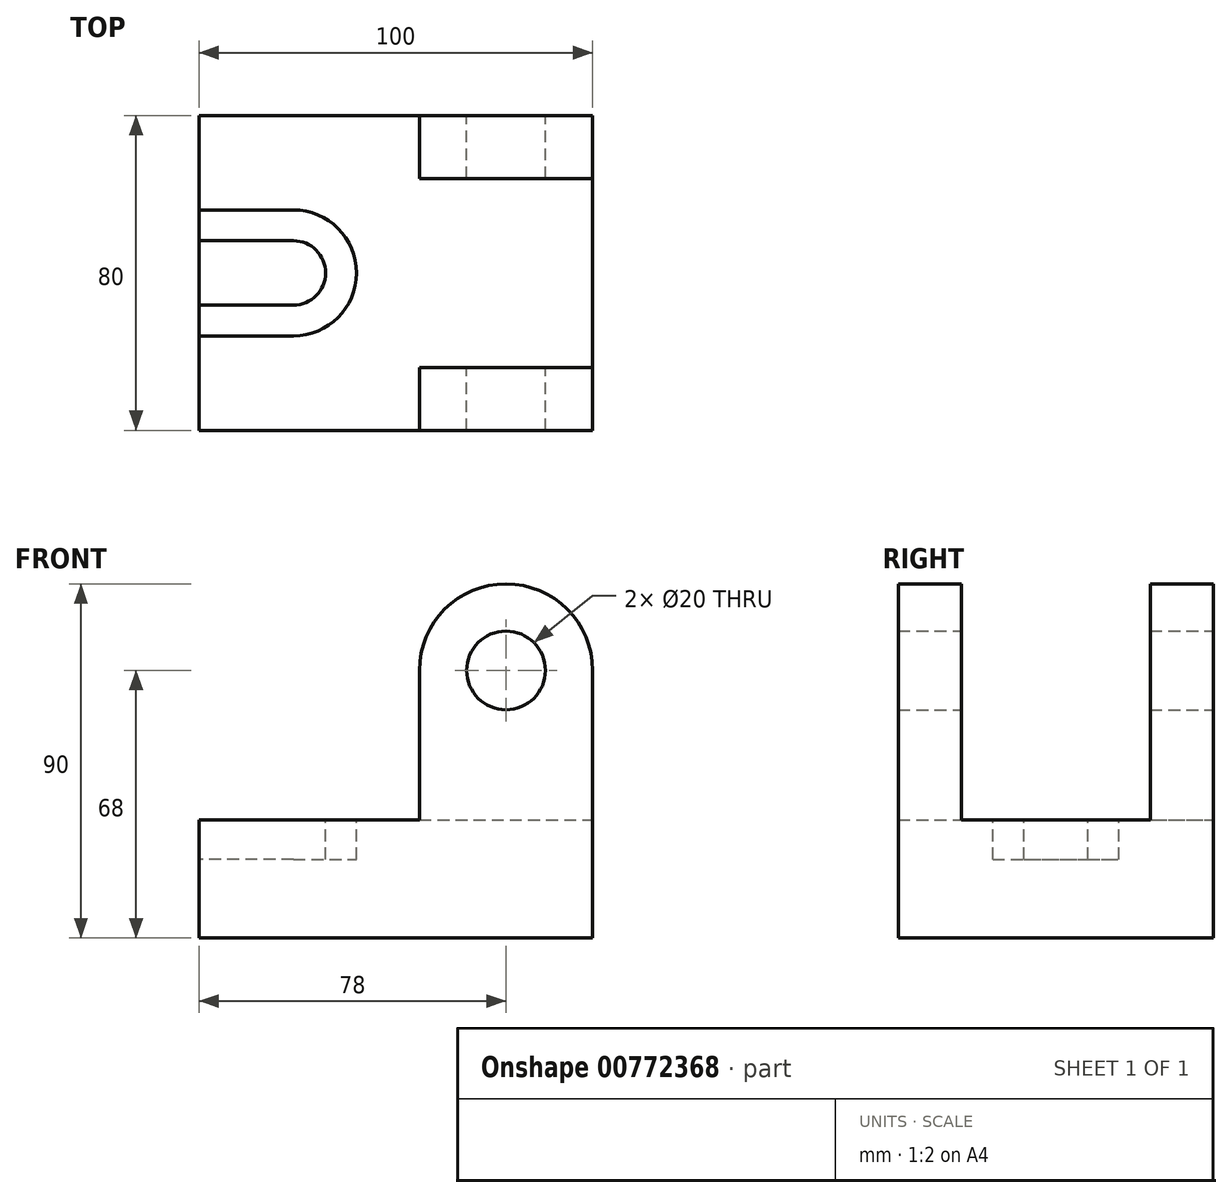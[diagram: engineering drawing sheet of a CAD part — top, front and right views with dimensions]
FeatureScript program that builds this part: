
annotation { "Feature Type Name" : "Feature", "Feature Type Description" : "" }
export const myFeature = defineFeature(function(context is Context, id is Id, definition is map)
    precondition{}
    {
        {
            var Q0;
            Q0=qCreatedBy(makeId("Front.planeOp"),FACE);
            var sketch = newSketch(context, id + "F0", { "sketchPlane" : qUnion([Q0])});
            skLineSegment(sketch, "E0", {"start": v(0, 0) * mm, "end": v(0, 68) * mm});
            skLineSegment(sketch, "E1", {"start": v(0, 0) * mm, "end": v(-100, 0) * mm});
            skLineSegment(sketch, "E2", {"start": v(-100, 0) * mm, "end": v(-100, 30) * mm});
            skLineSegment(sketch, "E3", {"start": v(-100, 30) * mm, "end": v(-44, 30) * mm});
            skLineSegment(sketch, "E4", {"start": v(-44, 30) * mm, "end": v(-44, 68) * mm});
            skArc(sketch, "E5", {"start": v(0, 68) * mm, "mid": v(-22, 90) * mm, "end": v(-44, 68) * mm});
            skCircle(sketch, "E6", {"center": v(-22, 68) * mm, "radius": 10 * mm});
            skLineSegment(sketch, "E7", {"start": v(-44, 30) * mm, "end": v(0, 30) * mm});
            skSolve(sketch);
        }
        {
            var Q0;
            Q0=makeQuery(id+"F0.imprint","IMPRINT",FACE,{"disambiguationData":[TD([[makeQuery(id+"F0.imprint","IMPRINT",EDGE,{"derivedFrom":sQuery(id+"F0.wireOp",EDGE,"E0")}),1.0]])]});
            extrude(context, id + "F1", {"entities" : qUnion([Q0]), "endBound" : BoundingType.SYMMETRIC, "depth" : 80 * mm, "offsetDistance" : 25 * mm});
        }
        {
            var Q0;
            Q0=makeQuery(id+"F0.imprint","IMPRINT",FACE,{"disambiguationData":[TD([[makeQuery(id+"F0.imprint","IMPRINT",EDGE,{"derivedFrom":sQuery(id+"F0.wireOp",EDGE,"E4")}),-1.0]])]});
            extrude(context, id + "F2", {"entities" : qUnion([Q0]), "operationType" : NewBodyOperationType.REMOVE, "endBound" : BoundingType.SYMMETRIC, "depth" : 48 * mm, "offsetDistance" : 25 * mm});
        }
        {
            var Q0;
            Q0=makeQuery(id+"F2.boolean.opBoolean","MERGE",FACE,{"derivedFrom":[makeQuery(id+"F1.opExtrude","SWEPT_FACE",FACE,{"disambiguationData":[OSD([sQuery(id+"F0.wireOp",EDGE,"E3")])]}),makeQuery(id+"F2.opExtrude","SWEPT_FACE",FACE,{"disambiguationData":[OSD([sQuery(id+"F0.wireOp",EDGE,"E7")])]})]});
            var sketch = newSketch(context, id + "F3", { "sketchPlane" : qUnion([Q0])});
            skLineSegment(sketch, "E8", {"start": v(-100, 0) * mm, "end": v(-76, 0) * mm, "construction": true});
            skArc(sketch, "E9", {"start": v(-76, -16) * mm, "mid": v(-60, 0) * mm, "end": v(-76, 16) * mm});
            skLineSegment(sketch, "E10", {"start": v(-76, 16) * mm, "end": v(-100, 16) * mm});
            skLineSegment(sketch, "E11", {"start": v(-76, -16) * mm, "end": v(-100, -16) * mm});
            skLineSegment(sketch, "E12.0", {"start": v(-76, 8.16) * mm, "end": v(-100, 8.16) * mm});
            skArc(sketch, "E12.1", {"start": v(-76, -8.16) * mm, "mid": v(-67.84, 0) * mm, "end": v(-76, 8.16) * mm});
            skLineSegment(sketch, "E12.2", {"start": v(-76, -8.16) * mm, "end": v(-100, -8.16) * mm});
            skSolve(sketch);
        }
        {
            var Q0;
            Q0=makeQuery(id+"F3.imprint","IMPRINT",FACE,{"disambiguationData":[TD([[makeQuery(id+"F3.imprint","IMPRINT",EDGE,{"derivedFrom":sQuery(id+"F3.wireOp",EDGE,"E9")}),1.0]])]});
            extrude(context, id + "F4", {"entities" : qUnion([Q0]), "operationType" : NewBodyOperationType.REMOVE, "oppositeDirection" : true, "depth" : 10 * mm, "offsetDistance" : 25 * mm});
        }
    });
